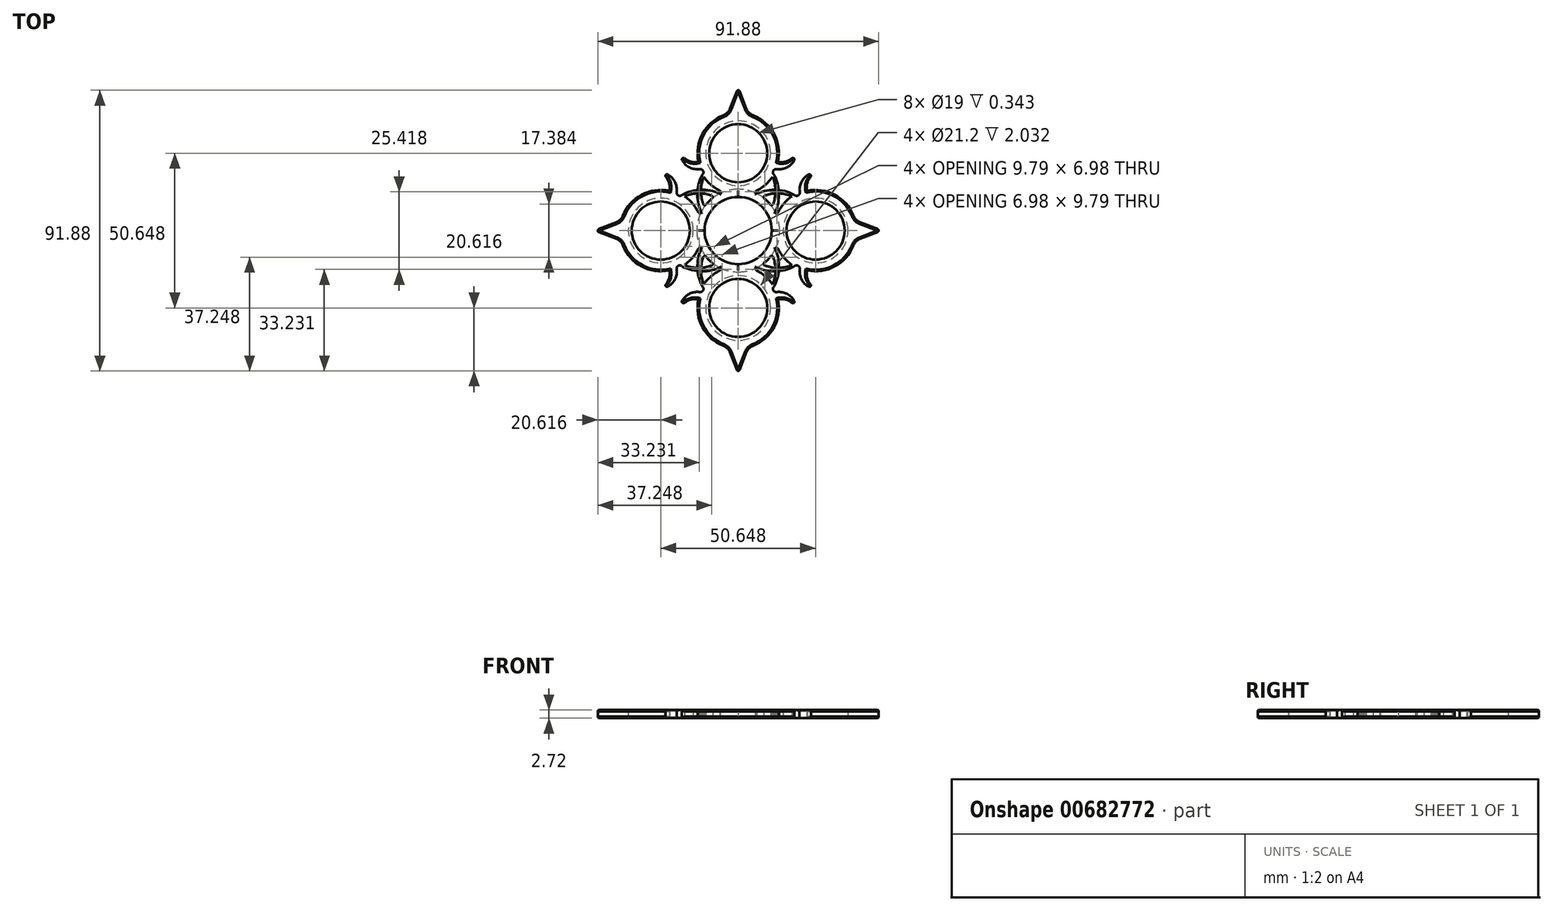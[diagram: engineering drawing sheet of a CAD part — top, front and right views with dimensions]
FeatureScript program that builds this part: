
annotation { "Feature Type Name" : "Feature", "Feature Type Description" : "" }
export const myFeature = defineFeature(function(context is Context, id is Id, definition is map)
    precondition{}
    {
        {
            var Q0;
            Q0=qCreatedBy(makeId("Top.planeOp"),FACE);
            var sketch = newSketch(context, id + "F0", { "sketchPlane" : qUnion([Q0])});
            skArc(sketch, "E0", {"start": v(0, 11) * mm, "mid": v(-11, 0) * mm, "end": v(0, -11) * mm});
            skArc(sketch, "E1", {"start": v(-12.62, -4.95) * mm, "mid": v(-10.66, -8.37) * mm, "end": v(-7.81, -11.07) * mm});
            skArc(sketch, "E2", {"start": v(-12.62, 4.95) * mm, "mid": v(-14.64, 8.47) * mm, "end": v(-17.6, 11.24) * mm});
            skLineSegment(sketch, "E3", {"start": v(0, 13.55) * mm, "end": v(0, 11) * mm});
            skArc(sketch, "E4.trimOffspring", {"start": v(0, 13.55) * mm, "mid": v(-3.11, 13.2) * mm, "end": v(-6.06, 12.12) * mm});
            skLineSegment(sketch, "E5.trimOffspring", {"start": v(0, -11) * mm, "end": v(0, -13.55) * mm});
            skPoint(sketch, "E6.centerSnap0", {"position": v(-11, 0) * mm});
            skArc(sketch, "E7", {"start": v(-17.6, -11.24) * mm, "mid": v(-12.7, -12.18) * mm, "end": v(-7.81, -11.07) * mm});
            skArc(sketch, "E8.trimOffspring", {"start": v(-7.81, 11.07) * mm, "mid": v(-10.66, 8.37) * mm, "end": v(-12.62, 4.95) * mm});
            skArc(sketch, "E9.trimOffspring", {"start": v(-6.06, 12.12) * mm, "mid": v(-12.21, 13.34) * mm, "end": v(-18.28, 11.74) * mm});
            skArc(sketch, "E10.trimOffspring", {"start": v(-7.81, 11.07) * mm, "mid": v(-12.7, 12.18) * mm, "end": v(-17.6, 11.24) * mm});
            skArc(sketch, "E11.trimOffspring", {"start": v(-6.06, -12.12) * mm, "mid": v(-3.11, -13.2) * mm, "end": v(0, -13.55) * mm});
            skArc(sketch, "E12.trimOffspring", {"start": v(-17.6, -11.24) * mm, "mid": v(-14.64, -8.47) * mm, "end": v(-12.62, -4.95) * mm});
            skArc(sketch, "E13", {"start": v(-20.15, 12.53) * mm, "mid": v(-21.48, 17.1) * mm, "end": v(-25.8, 19.05) * mm});
            skArc(sketch, "E14", {"start": v(-22.53, 13) * mm, "mid": v(-23.02, 16.65) * mm, "end": v(-25.8, 19.05) * mm});
            skPoint(sketch, "E15.orphan", {"position": v(-25.8, 9.28) * mm});
            skArc(sketch, "E16.trimOffspring", {"start": v(-22.53, 13) * mm, "mid": v(-31.62, 11.72) * mm, "end": v(-37.72, 4.85) * mm});
            skArc(sketch, "E17.MirrorCS", {"start": v(-22.53, -13) * mm, "mid": v(-23.02, -16.65) * mm, "end": v(-25.8, -19.05) * mm});
            skArc(sketch, "E18.MirrorCS", {"start": v(-20.15, -12.53) * mm, "mid": v(-21.48, -17.1) * mm, "end": v(-25.8, -19.05) * mm});
            skArc(sketch, "E19", {"start": v(-18.28, -11.74) * mm, "mid": v(-19.55, -11.48) * mm, "end": v(-20.13, -12.64) * mm});
            skArc(sketch, "E20.trimOffspring", {"start": v(-18.28, -11.74) * mm, "mid": v(-12.21, -13.34) * mm, "end": v(-6.06, -12.12) * mm});
            skPoint(sketch, "E21.orphan", {"position": v(-20.43, -11.4) * mm});
            skArc(sketch, "E22.MirrorCS", {"start": v(-18.28, 11.74) * mm, "mid": v(-19.55, 11.48) * mm, "end": v(-20.13, 12.64) * mm});
            skPoint(sketch, "E23.trimOffspring.end.orphan", {"position": v(-20.43, 11.4) * mm});
            skCircle(sketch, "E24", {"center": v(-25.32, 0) * mm, "radius": 9.5 * mm});
            skLineSegment(sketch, "E25", {"start": v(-46.84, 0) * mm, "end": v(-39.9, 2.68) * mm});
            skLineSegment(sketch, "E26.MirrorCS", {"start": v(-46.84, 0) * mm, "end": v(-39.9, -2.68) * mm});
            skArc(sketch, "E27.trimOffspring", {"start": v(-37.72, -4.85) * mm, "mid": v(-31.62, -11.72) * mm, "end": v(-22.53, -13) * mm});
            skPoint(sketch, "E28.visualSharp", {"position": v(-38.21, -3.33) * mm});
            skArc(sketch, "E28.filletArc", {"start": v(-37.72, -4.85) * mm, "mid": v(-38.58, -3.53) * mm, "end": v(-39.9, -2.68) * mm});
            skPoint(sketch, "E29.visualSharp", {"position": v(-38.21, 3.33) * mm});
            skArc(sketch, "E29.filletArc", {"start": v(-39.9, 2.68) * mm, "mid": v(-38.58, 3.53) * mm, "end": v(-37.72, 4.85) * mm});
            skSolve(sketch);
        }
        {
            var Q0;
            Q0=makeQuery(id+"F0.imprint","IMPRINT",FACE,{"disambiguationData":[TD([[makeQuery(id+"F0.imprint","IMPRINT",EDGE,{"derivedFrom":sQuery(id+"F0.wireOp",EDGE,"E0")}),-1.0]])]});
            extrude(context, id + "F1", {"entities" : qUnion([Q0]), "endBound" : BoundingType.SYMMETRIC, "depth" : 2.72 * mm, "offsetDistance" : 25.4 * mm});
        }
        {
            var Q0;
            Q0=qCreatedBy(makeId("Top.planeOp"),FACE);
            var sketch = newSketch(context, id + "F2", { "sketchPlane" : qUnion([Q0])});
            skCircle(sketch, "E30", {"center": v(-25.32, 0) * mm, "radius": 10.6 * mm});
            skSolve(sketch);
        }
        {
            var Q0;
            Q0=makeQuery(id+"F2.imprint","IMPRINT",FACE,{"disambiguationData":[TD([[makeQuery(id+"F2.imprint","IMPRINT",EDGE,{"derivedFrom":sQuery(id+"F2.wireOp",EDGE,"E30")}),1.0]])]});
            extrude(context, id + "F3", {"entities" : qUnion([Q0]), "operationType" : NewBodyOperationType.REMOVE, "endBound" : BoundingType.SYMMETRIC, "depth" : 2.03 * mm, "offsetDistance" : 25.4 * mm});
        }
        {
            var Q0;
            Q0=makeQuery(id+"F1.opExtrude","CAP_EDGE",EDGE,{"disambiguationData":[OSD([sQuery(id+"F0.wireOp",EDGE,"E16.trimOffspring")])],"isStart":false});
            var Q1;
            Q1=makeQuery(id+"F1.opExtrude","CAP_EDGE",EDGE,{"disambiguationData":[OSD([sQuery(id+"F0.wireOp",EDGE,"E16.trimOffspring")])],"isStart":true});
            var Q2;
            Q2=makeQuery(id+"F1.opExtrude","CAP_EDGE",EDGE,{"disambiguationData":[OSD([sQuery(id+"F0.wireOp",EDGE,"E14")])],"isStart":true});
            var Q3;
            Q3=makeQuery(id+"F1.opExtrude","CAP_EDGE",EDGE,{"disambiguationData":[OSD([sQuery(id+"F0.wireOp",EDGE,"E14")])],"isStart":false});
            var Q4;
            Q4=makeQuery(id+"F1.opExtrude","CAP_EDGE",EDGE,{"disambiguationData":[OSD([sQuery(id+"F0.wireOp",EDGE,"E27.trimOffspring")])],"isStart":false});
            var Q5;
            Q5=makeQuery(id+"F1.opExtrude","CAP_EDGE",EDGE,{"disambiguationData":[OSD([sQuery(id+"F0.wireOp",EDGE,"E27.trimOffspring")])],"isStart":true});
            var Q6;
            Q6=makeQuery(id+"F1.opExtrude","CAP_EDGE",EDGE,{"disambiguationData":[OSD([sQuery(id+"F0.wireOp",EDGE,"E17.MirrorCS")])],"isStart":true});
            var Q7;
            Q7=makeQuery(id+"F1.opExtrude","CAP_EDGE",EDGE,{"disambiguationData":[OSD([sQuery(id+"F0.wireOp",EDGE,"E17.MirrorCS")])],"isStart":false});
            chamfer(context, id + "F4", {"entities" : qUnion([Q0, Q1, Q2, Q3, Q4, Q5, Q6, Q7]), "width" : 0.5 * mm, "tangentPropagation" : true});
        }
        {
            var Q0;
            Q0=makeQuery(id+"F1.opExtrude","SWEPT_EDGE",EDGE,{"disambiguationData":[OSD([sQuery(id+"F0.wireOp",EDGE,"E25"),sQuery(id+"F0.wireOp",EDGE,"E26.MirrorCS")])]});
            var Q1;
            Q1=makeQuery(id+"F1.opExtrude","SWEPT_EDGE",EDGE,{"disambiguationData":[OSD([sQuery(id+"F0.wireOp",EDGE,"E17.MirrorCS"),sQuery(id+"F0.wireOp",EDGE,"E18.MirrorCS")])]});
            var Q2;
            Q2=makeQuery(id+"F1.opExtrude","SWEPT_EDGE",EDGE,{"disambiguationData":[OSD([sQuery(id+"F0.wireOp",EDGE,"E13"),sQuery(id+"F0.wireOp",EDGE,"E14")])]});
            var Q3;
            Q3=makeQuery(id+"F1.opExtrude","SWEPT_FACE",FACE,{"disambiguationData":[OSD([sQuery(id+"F0.wireOp",EDGE,"E1")])]});
            var Q4;
            Q4=makeQuery(id+"F1.opExtrude","SWEPT_FACE",FACE,{"disambiguationData":[OSD([sQuery(id+"F0.wireOp",EDGE,"E8.trimOffspring")])]});
            var Q5;
            Q5=makeQuery(id+"F1.opExtrude","CAP_EDGE",EDGE,{"disambiguationData":[OSD([sQuery(id+"F0.wireOp",EDGE,"E11.trimOffspring")])],"isStart":false});
            var Q6;
            Q6=makeQuery(id+"F1.opExtrude","CAP_EDGE",EDGE,{"disambiguationData":[OSD([sQuery(id+"F0.wireOp",EDGE,"E11.trimOffspring")])],"isStart":true});
            var Q7;
            Q7=makeQuery(id+"F1.opExtrude","CAP_EDGE",EDGE,{"disambiguationData":[OSD([sQuery(id+"F0.wireOp",EDGE,"E0")])],"isStart":false});
            var Q8;
            Q8=makeQuery(id+"F1.opExtrude","CAP_EDGE",EDGE,{"disambiguationData":[OSD([sQuery(id+"F0.wireOp",EDGE,"E0")])],"isStart":true});
            var Q9;
            Q9=makeQuery(id+"F1.opExtrude","CAP_EDGE",EDGE,{"disambiguationData":[OSD([sQuery(id+"F0.wireOp",EDGE,"E4.trimOffspring")])],"isStart":false});
            var Q10;
            Q10=makeQuery(id+"F1.opExtrude","CAP_EDGE",EDGE,{"disambiguationData":[OSD([sQuery(id+"F0.wireOp",EDGE,"E4.trimOffspring")])],"isStart":true});
            var Q11;
            Q11=makeQuery(id+"F1.opExtrude","CAP_EDGE",EDGE,{"disambiguationData":[OSD([sQuery(id+"F0.wireOp",EDGE,"E22.MirrorCS")])],"isStart":false});
            fillet(context, id + "F5", {"entities" : qUnion([Q0, Q1, Q2, Q3, Q4, Q5, Q6, Q7, Q8, Q9, Q10, Q11]), "radius" : 0.5 * mm, "tangentPropagation" : true, "allowEdgeOverflow" : false});
        }
        {
            var Q0;
            Q0=makeQuery(id+"F1.opExtrude","SWEPT_BODY",BODY,{"disambiguationData":[OSD([sQuery(id+"F0.wireOp",EDGE,"E0"),sQuery(id+"F0.wireOp",EDGE,"E1"),sQuery(id+"F0.wireOp",EDGE,"E2"),sQuery(id+"F0.wireOp",EDGE,"E3"),sQuery(id+"F0.wireOp",EDGE,"E4.trimOffspring"),sQuery(id+"F0.wireOp",EDGE,"E5.trimOffspring"),sQuery(id+"F0.wireOp",EDGE,"E7"),sQuery(id+"F0.wireOp",EDGE,"E8.trimOffspring"),sQuery(id+"F0.wireOp",EDGE,"E9.trimOffspring"),sQuery(id+"F0.wireOp",EDGE,"E10.trimOffspring"),sQuery(id+"F0.wireOp",EDGE,"E11.trimOffspring"),sQuery(id+"F0.wireOp",EDGE,"E12.trimOffspring"),sQuery(id+"F0.wireOp",EDGE,"E13"),sQuery(id+"F0.wireOp",EDGE,"E14"),sQuery(id+"F0.wireOp",EDGE,"E16.trimOffspring"),sQuery(id+"F0.wireOp",EDGE,"E17.MirrorCS"),sQuery(id+"F0.wireOp",EDGE,"E18.MirrorCS"),sQuery(id+"F0.wireOp",EDGE,"E19"),sQuery(id+"F0.wireOp",EDGE,"E20.trimOffspring"),sQuery(id+"F0.wireOp",EDGE,"E22.MirrorCS"),sQuery(id+"F0.wireOp",EDGE,"E24"),sQuery(id+"F0.wireOp",EDGE,"E25"),sQuery(id+"F0.wireOp",EDGE,"E26.MirrorCS"),sQuery(id+"F0.wireOp",EDGE,"E27.trimOffspring"),sQuery(id+"F0.wireOp",EDGE,"E28.filletArc"),sQuery(id+"F0.wireOp",EDGE,"E29.filletArc")])]});
            var Q1;
            Q1=makeQuery(id+"F1.opExtrude","SWEPT_FACE",FACE,{"disambiguationData":[OSD([sQuery(id+"F0.wireOp",EDGE,"E0")])]});
            circularPattern(context, id + "F6", {"entities" : qUnion([Q0]), "axis" : qUnion([Q1]), "angle" : 360 * degree, "instanceCount" : 4, "equalSpace" : true});
        }
    });
